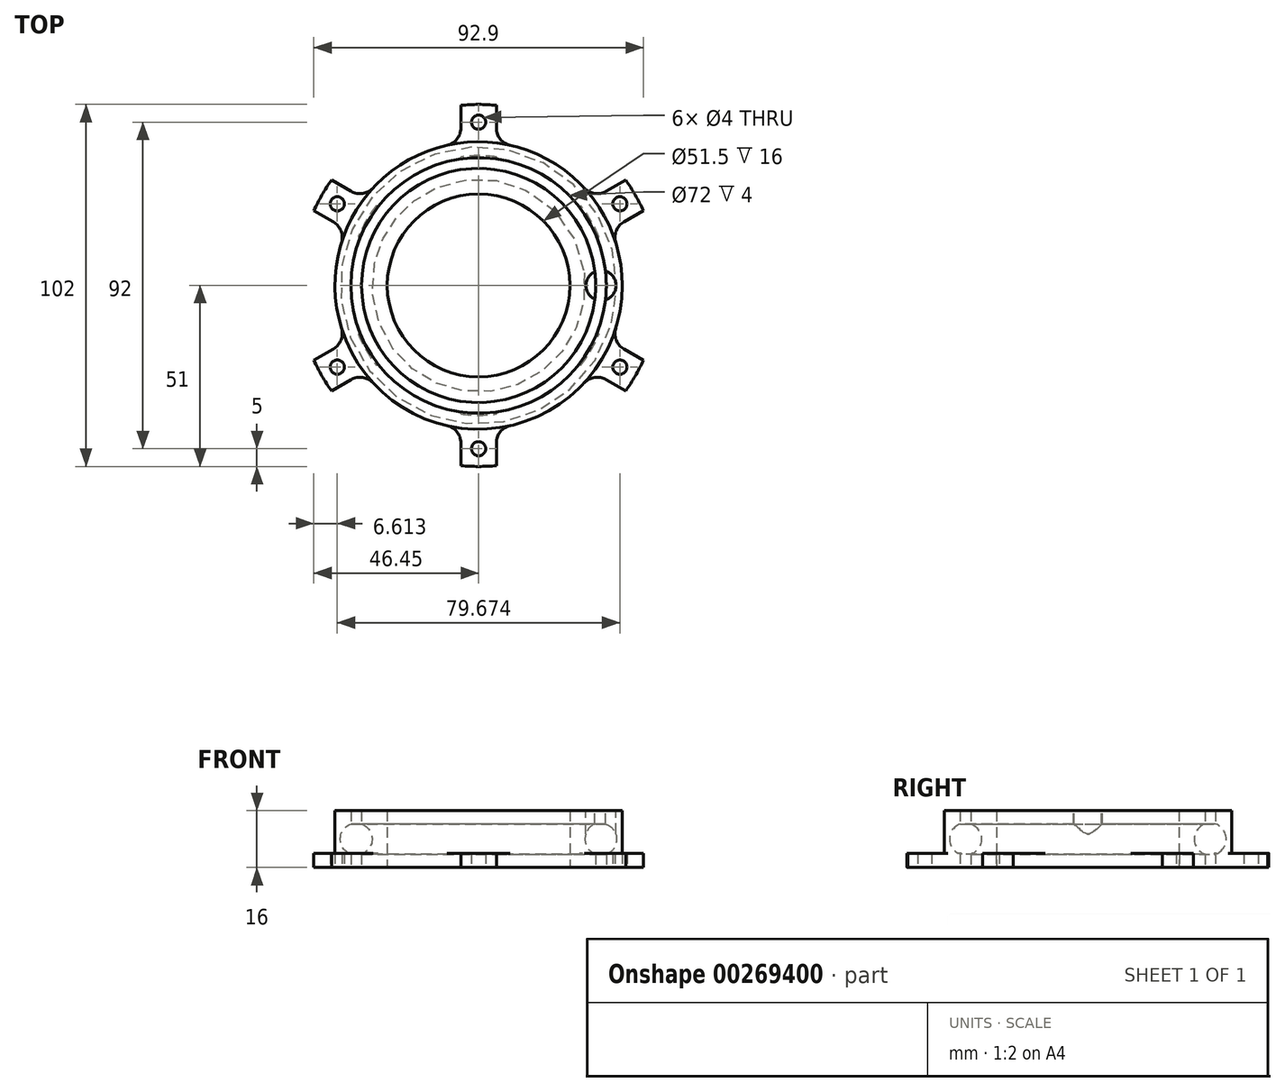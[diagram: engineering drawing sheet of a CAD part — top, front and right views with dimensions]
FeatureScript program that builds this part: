
annotation { "Feature Type Name" : "Feature", "Feature Type Description" : "" }
export const myFeature = defineFeature(function(context is Context, id is Id, definition is map)
    precondition{}
    {
        {
            var Q0;
            Q0=qCreatedBy(makeId("Top.planeOp"),FACE);
            var sketch = newSketch(context, id + "F0", { "sketchPlane" : qUnion([Q0])});
            skCircle(sketch, "E0", {"center": v(0, 0) * mm, "radius": 25.75 * mm});
            skCircle(sketch, "E1", {"center": v(0, 0) * mm, "radius": 40.5 * mm});
            skCircle(sketch, "E2", {"center": v(0, 0) * mm, "radius": 33 * mm});
            skCircle(sketch, "E3", {"center": v(0, 0) * mm, "radius": 36 * mm});
            skPoint(sketch, "E4", {"position": v(0, 50.94) * mm});
            skSolve(sketch);
        }
        {
            var Q0;
            Q0=makeQuery(id+"F0.imprint","IMPRINT",FACE,{"disambiguationData":[TD([[makeQuery(id+"F0.imprint","IMPRINT",EDGE,{"derivedFrom":sQuery(id+"F0.wireOp",EDGE,"E1")}),1.0]])]});
            var Q1;
            Q1=makeQuery(id+"F0.imprint","IMPRINT",FACE,{"disambiguationData":[TD([[makeQuery(id+"F0.imprint","IMPRINT",EDGE,{"derivedFrom":sQuery(id+"F0.wireOp",EDGE,"E0")}),-1.0]])]});
            extrude(context, id + "F1", {"entities" : qUnion([Q0, Q1]), "depth" : 16 * mm});
        }
        {
            var Q0;
            Q0=qCreatedBy(makeId("Right.planeOp"),FACE);
            var sketch = newSketch(context, id + "F2", { "sketchPlane" : qUnion([Q0])});
            skLineSegment(sketch, "E5", {"start": v(0, 0) * mm, "end": v(0, 16) * mm});
            skPoint(sketch, "E6", {"position": v(0, 8) * mm});
            skSolve(sketch);
        }
        {
            var Q0;
            Q0=makeQuery(id+"F1.opExtrude","CAP_FACE",FACE,{"disambiguationData":[OSD([sQuery(id+"F0.wireOp",EDGE,"E0"),sQuery(id+"F0.wireOp",EDGE,"E2")])],"isStart":false});
            var sketch = newSketch(context, id + "F3", { "sketchPlane" : qUnion([Q0])});
            skPoint(sketch, "E7", {"position": v(0, -33) * mm});
            skPoint(sketch, "E8", {"position": v(0, -36) * mm});
            skSolve(sketch);
        }
        {
            var Q0;
            Q0=qCreatedBy(makeId("Right.planeOp"),FACE);
            var sketch = newSketch(context, id + "F4", { "sketchPlane" : qUnion([Q0])});
            skCircle(sketch, "E9", {"center": v(-34.5, 8) * mm, "radius": 4.5 * mm});
            skLineSegment(sketch, "E10", {"start": v(-36, 16) * mm, "end": v(-36, 0) * mm});
            skSolve(sketch);
        }
        {
            var Q0;
            Q0=qCreatedBy(makeId("Right.planeOp"),FACE);
            var sketch = newSketch(context, id + "F5", { "sketchPlane" : qUnion([Q0])});
            skLineSegment(sketch, "E11", {"start": v(-34.5, 11.25) * mm, "end": v(-34.5, 4.75) * mm});
            skPoint(sketch, "E12", {"position": v(0, 5) * mm});
            skPoint(sketch, "E13", {"position": v(-34.5, 8) * mm});
            skArc(sketch, "E14", {"start": v(-34.5, 11.25) * mm, "mid": v(-37.75, 8) * mm, "end": v(-34.5, 4.75) * mm});
            skSolve(sketch);
        }
        {
            var Q0;
            Q0=makeQuery(id+"F4.imprint","IMPRINT",FACE,{"disambiguationData":[TD([[makeQuery(id+"F4.imprint","IMPRINT",EDGE,{"derivedFrom":sQuery(id+"F4.wireOp",EDGE,"E9")}),1.0]])]});
            var Q1;
            Q1=makeQuery(id+"F1.opExtrude","SWEPT_FACE",FACE,{"disambiguationData":[OSD([sQuery(id+"F0.wireOp",EDGE,"E2")])]});
            revolve(context, id + "F6", {"operationType" : NewBodyOperationType.REMOVE, "entities" : qUnion([Q0]), "axis" : qUnion([Q1]), "revolveType" : RevolveType.FULL, "oppositeDirection" : true});
        }
        {
            var Q0;
            Q0=qCreatedBy(makeId("Top.planeOp"),FACE);
            cPlane(context, id + "F7", {"entities" : qUnion([Q0]), "cplaneType" : CPlaneType.OFFSET, "offset" : 5 * mm, "width" : 150 * mm, "height" : 150 * mm});
        }
        {
            var Q0;
            Q0=makeQuery(id+"F1.opExtrude","CAP_FACE",FACE,{"disambiguationData":[OSD([sQuery(id+"F0.wireOp",EDGE,"E1"),sQuery(id+"F0.wireOp",EDGE,"E3")])],"isStart":false});
            var sketch = newSketch(context, id + "F8", { "sketchPlane" : qUnion([Q0])});
            skCircle(sketch, "E15", {"center": v(34.5, 0) * mm, "radius": 4.25 * mm});
            skSolve(sketch);
        }
        {
            var Q0;
            Q0=makeQuery(id+"F8.imprint","IMPRINT",FACE,{"disambiguationData":[TD([[makeQuery(id+"F8.imprint","IMPRINT",EDGE,{"derivedFrom":sQuery(id+"F8.wireOp",EDGE,"E15")}),1.0]])]});
            extrude(context, id + "F9", {"entities" : qUnion([Q0]), "operationType" : NewBodyOperationType.REMOVE, "oppositeDirection" : true, "depth" : 8 * mm});
        }
        {
            var Q0;
            Q0=makeQuery(id+"F1.opExtrude","CAP_FACE",FACE,{"disambiguationData":[OSD([sQuery(id+"F0.wireOp",EDGE,"E1"),sQuery(id+"F0.wireOp",EDGE,"E3")])],"isStart":true});
            var sketch = newSketch(context, id + "F10", { "sketchPlane" : qUnion([Q0])});
            skPoint(sketch, "E16", {"position": v(0, 46) * mm});
            skCircle(sketch, "E17", {"center": v(0, 0) * mm, "radius": 51 * mm});
            skLineSegment(sketch, "E18", {"start": v(-5, 50.75) * mm, "end": v(-5, 35.65) * mm});
            skLineSegment(sketch, "E19", {"start": v(5, 50.75) * mm, "end": v(5, 35.65) * mm});
            skSolve(sketch);
        }
        {
            var Q0;
            {var subQ0=sQuery(id+"F10.wireOp",EDGE,"E18");var subQ1=makeQuery(id+"F1.opExtrude","CAP_EDGE",EDGE,{"disambiguationData":[OSD([sQuery(id+"F0.wireOp",EDGE,"E3")])],"isStart":true});var subQ2=makeQuery(id+"F10.imprint","INTERSECT",VERTEX,{"derivedFrom":[subQ1,subQ0]});Q0=makeQuery(id+"F10.imprint","IMPRINT",FACE,{"disambiguationData":[TD([[makeQuery(id+"F10.imprint","IMPRINT",EDGE,{"disambiguationData":[TD([[subQ2,1.0]])],"derivedFrom":subQ0}),1.0]])]});}
            var Q1;
            {var subQ0=sQuery(id+"F10.wireOp",EDGE,"E18");var subQ1=sQuery(id+"F10.wireOp",EDGE,"E17");var subQ2=makeQuery(id+"F10.imprint","INTERSECT",VERTEX,{"derivedFrom":[subQ1,subQ0]});Q1=makeQuery(id+"F10.imprint","IMPRINT",FACE,{"disambiguationData":[TD([[makeQuery(id+"F10.imprint","IMPRINT",EDGE,{"disambiguationData":[TD([[subQ2,1.0]])],"derivedFrom":subQ1}),1.0]])]});}
            extrude(context, id + "F11", {"entities" : qUnion([Q0, Q1]), "oppositeDirection" : true, "depth" : 4 * mm});
        }
        {
            var Q0;
            Q0=sQuery(id+"F10.wireOp",VERTEX,"E16");
            var Q1;
            Q1=makeQuery(id+"F11.opExtrude","SWEPT_BODY",BODY,{"disambiguationData":[OSD([sQuery(id+"F0.wireOp",EDGE,"E3"),sQuery(id+"F10.wireOp",EDGE,"E17"),sQuery(id+"F10.wireOp",EDGE,"E18"),sQuery(id+"F10.wireOp",EDGE,"E19")])]});
            hole(context, id + "F12", {"style" : HoleStyle.SIMPLE, "endStyle" : HoleEndStyle.THROUGH, "holeDiameter" : 4 * mm, "tappedDepth" : 12 * mm, "tapClearance" : 3, "locations" : qUnion([Q0]), "scope" : qUnion([Q1])});
        }
        {
            var Q0;
            Q0=makeQuery(id+"F11.opExtrude","SWEPT_BODY",BODY,{"disambiguationData":[OSD([sQuery(id+"F0.wireOp",EDGE,"E3"),sQuery(id+"F10.wireOp",EDGE,"E17"),sQuery(id+"F10.wireOp",EDGE,"E18"),sQuery(id+"F10.wireOp",EDGE,"E19")])]});
            var Q1;
            Q1=makeQuery(id+"F1.opExtrude","CAP_EDGE",EDGE,{"disambiguationData":[OSD([sQuery(id+"F0.wireOp",EDGE,"E1")])],"isStart":true});
            circularPattern(context, id + "F13", {"operationType" : NewBodyOperationType.ADD, "entities" : qUnion([Q0]), "axis" : qUnion([Q1]), "angle" : 360 * degree, "instanceCount" : 6, "equalSpace" : true});
        }
        {
            var Q0;
            Q0=makeQuery(id+"F13.boolean.opBoolean","INTERSECT",EDGE,{"derivedFrom":[makeQuery(id+"F1.opExtrude","SWEPT_FACE",FACE,{"disambiguationData":[OSD([sQuery(id+"F0.wireOp",EDGE,"E1")])]}),makeQuery(id+"F11.opExtrude","SWEPT_FACE",FACE,{"disambiguationData":[OSD([sQuery(id+"F10.wireOp",EDGE,"E19")])]})]});
            var Q1;
            Q1=makeQuery(id+"F13.boolean.opBoolean","INTERSECT",EDGE,{"derivedFrom":[makeQuery(id+"F1.opExtrude","SWEPT_FACE",FACE,{"disambiguationData":[OSD([sQuery(id+"F0.wireOp",EDGE,"E1")])]}),makeQuery(id+"F11.opExtrude","SWEPT_FACE",FACE,{"disambiguationData":[OSD([sQuery(id+"F10.wireOp",EDGE,"E18")])]})]});
            var Q2;
            Q2=makeQuery(id+"F13.boolean.opBoolean","INTERSECT",EDGE,{"derivedFrom":[makeQuery(id+"F1.opExtrude","SWEPT_FACE",FACE,{"disambiguationData":[OSD([sQuery(id+"F0.wireOp",EDGE,"E1")])]}),makeQuery(id+"F13.opPattern","COPY",FACE,{"derivedFrom":makeQuery(id+"F11.opExtrude","SWEPT_FACE",FACE,{"disambiguationData":[OSD([sQuery(id+"F10.wireOp",EDGE,"E18")])]}),"instanceName":"5"})]});
            var Q3;
            Q3=makeQuery(id+"F13.boolean.opBoolean","INTERSECT",EDGE,{"derivedFrom":[makeQuery(id+"F1.opExtrude","SWEPT_FACE",FACE,{"disambiguationData":[OSD([sQuery(id+"F0.wireOp",EDGE,"E1")])]}),makeQuery(id+"F13.opPattern","COPY",FACE,{"derivedFrom":makeQuery(id+"F11.opExtrude","SWEPT_FACE",FACE,{"disambiguationData":[OSD([sQuery(id+"F10.wireOp",EDGE,"E19")])]}),"instanceName":"5"})]});
            var Q4;
            Q4=makeQuery(id+"F13.boolean.opBoolean","INTERSECT",EDGE,{"derivedFrom":[makeQuery(id+"F1.opExtrude","SWEPT_FACE",FACE,{"disambiguationData":[OSD([sQuery(id+"F0.wireOp",EDGE,"E1")])]}),makeQuery(id+"F13.opPattern","COPY",FACE,{"derivedFrom":makeQuery(id+"F11.opExtrude","SWEPT_FACE",FACE,{"disambiguationData":[OSD([sQuery(id+"F10.wireOp",EDGE,"E19")])]}),"instanceName":"4"})]});
            var Q5;
            Q5=makeQuery(id+"F13.boolean.opBoolean","INTERSECT",EDGE,{"derivedFrom":[makeQuery(id+"F1.opExtrude","SWEPT_FACE",FACE,{"disambiguationData":[OSD([sQuery(id+"F0.wireOp",EDGE,"E1")])]}),makeQuery(id+"F13.opPattern","COPY",FACE,{"derivedFrom":makeQuery(id+"F11.opExtrude","SWEPT_FACE",FACE,{"disambiguationData":[OSD([sQuery(id+"F10.wireOp",EDGE,"E18")])]}),"instanceName":"4"})]});
            var Q6;
            Q6=makeQuery(id+"F13.boolean.opBoolean","INTERSECT",EDGE,{"derivedFrom":[makeQuery(id+"F1.opExtrude","SWEPT_FACE",FACE,{"disambiguationData":[OSD([sQuery(id+"F0.wireOp",EDGE,"E1")])]}),makeQuery(id+"F13.opPattern","COPY",FACE,{"derivedFrom":makeQuery(id+"F11.opExtrude","SWEPT_FACE",FACE,{"disambiguationData":[OSD([sQuery(id+"F10.wireOp",EDGE,"E19")])]}),"instanceName":"3"})]});
            var Q7;
            Q7=makeQuery(id+"F13.boolean.opBoolean","INTERSECT",EDGE,{"derivedFrom":[makeQuery(id+"F1.opExtrude","SWEPT_FACE",FACE,{"disambiguationData":[OSD([sQuery(id+"F0.wireOp",EDGE,"E1")])]}),makeQuery(id+"F13.opPattern","COPY",FACE,{"derivedFrom":makeQuery(id+"F11.opExtrude","SWEPT_FACE",FACE,{"disambiguationData":[OSD([sQuery(id+"F10.wireOp",EDGE,"E19")])]}),"instanceName":"2"})]});
            var Q8;
            Q8=makeQuery(id+"F13.boolean.opBoolean","INTERSECT",EDGE,{"derivedFrom":[makeQuery(id+"F1.opExtrude","SWEPT_FACE",FACE,{"disambiguationData":[OSD([sQuery(id+"F0.wireOp",EDGE,"E1")])]}),makeQuery(id+"F13.opPattern","COPY",FACE,{"derivedFrom":makeQuery(id+"F11.opExtrude","SWEPT_FACE",FACE,{"disambiguationData":[OSD([sQuery(id+"F10.wireOp",EDGE,"E18")])]}),"instanceName":"3"})]});
            var Q9;
            Q9=makeQuery(id+"F13.boolean.opBoolean","INTERSECT",EDGE,{"derivedFrom":[makeQuery(id+"F1.opExtrude","SWEPT_FACE",FACE,{"disambiguationData":[OSD([sQuery(id+"F0.wireOp",EDGE,"E1")])]}),makeQuery(id+"F13.opPattern","COPY",FACE,{"derivedFrom":makeQuery(id+"F11.opExtrude","SWEPT_FACE",FACE,{"disambiguationData":[OSD([sQuery(id+"F10.wireOp",EDGE,"E18")])]}),"instanceName":"2"})]});
            var Q10;
            Q10=makeQuery(id+"F13.boolean.opBoolean","INTERSECT",EDGE,{"derivedFrom":[makeQuery(id+"F1.opExtrude","SWEPT_FACE",FACE,{"disambiguationData":[OSD([sQuery(id+"F0.wireOp",EDGE,"E1")])]}),makeQuery(id+"F13.opPattern","COPY",FACE,{"derivedFrom":makeQuery(id+"F11.opExtrude","SWEPT_FACE",FACE,{"disambiguationData":[OSD([sQuery(id+"F10.wireOp",EDGE,"E19")])]}),"instanceName":"1"})]});
            var Q11;
            Q11=makeQuery(id+"F13.boolean.opBoolean","INTERSECT",EDGE,{"derivedFrom":[makeQuery(id+"F1.opExtrude","SWEPT_FACE",FACE,{"disambiguationData":[OSD([sQuery(id+"F0.wireOp",EDGE,"E1")])]}),makeQuery(id+"F13.opPattern","COPY",FACE,{"derivedFrom":makeQuery(id+"F11.opExtrude","SWEPT_FACE",FACE,{"disambiguationData":[OSD([sQuery(id+"F10.wireOp",EDGE,"E18")])]}),"instanceName":"1"})]});
            fillet(context, id + "F14", {"entities" : qUnion([Q0, Q1, Q2, Q3, Q4, Q5, Q6, Q7, Q8, Q9, Q10, Q11]), "radius" : 5 * mm, "tangentPropagation" : true, "allowEdgeOverflow" : false});
        }
    });
